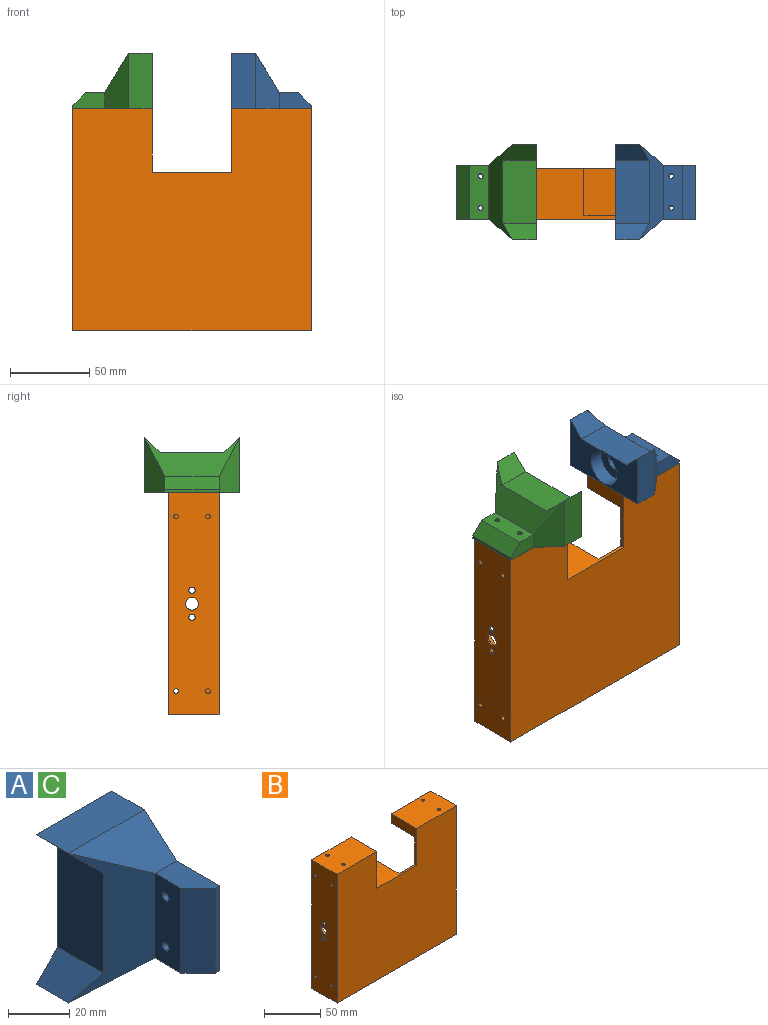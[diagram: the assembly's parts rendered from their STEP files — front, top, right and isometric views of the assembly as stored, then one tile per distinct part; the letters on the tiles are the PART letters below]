
ASSEMBLY  parts=3 mates=2
PART A: 21 faces, bbox 35x50x60 mm
  f0: plane 20x10mm, normal (0,0,-1), area 168mm2, adj f1,f2,f3,f4,f5
  f1: plane 34x2mm, normal (0,-1,0), area 68mm2, adj f0,f2,f3,f6
  f2: plane 34x8mm, normal (-0.71,-0.71,0), area 384.7mm2, adj f0,f1,f4,f6
  f3: plane 60x50mm, normal (1,0,0), area 2270.9mm2, adj f0,f1,f5,f6,f7,f8,f9,f10
  f4: plane 34x12mm, normal (-1,0,0), area 393.9mm2, adj f0,f2,f6,f11,f12,f13
  f5: plane 35x15mm, normal (0,-0.65,-0.76), area 446.6mm2, adj f0,f3,f8,f13
  f6: plane 20x10mm, normal (0,0,1), area 168mm2, adj f1,f2,f3,f4,f10
  f7: plane 60x35mm, normal (0,1,0), area 1184.5mm2, adj f3,f8,f9,f14,f15,f16,f17
  f8: plane 35x15mm, normal (0,0,-1), area 525mm2, adj f3,f5,f7,f14
  f9: plane 35x15mm, normal (0,0,1), area 525mm2, adj f3,f7,f10,f16
  f10: plane 35x15mm, normal (0,-0.65,0.76), area 446.6mm2, adj f3,f6,f9,f13
  f11: cylinder r=1.5mm len=10mm, axis (1,0,0), area 94.2mm2, adj f3,f4
  f12: cylinder r=1.5mm len=10mm, axis (1,0,0), area 94.2mm2, adj f3,f4
  f13: plane 60x25mm, normal (-0.51,-0.86,0), area 787.2mm2, adj f4,f5,f10,f14,f15,f16
  f14: plane 21x10mm, normal (-0.71,0,0.71), area 254.6mm2, adj f7,f8,f13,f15
  f15: plane 40x21mm, normal (-1,0,0), area 840mm2, adj f7,f13,f14,f16
  f16: plane 21x10mm, normal (-0.71,0,-0.71), area 254.6mm2, adj f7,f9,f13,f15
  f17: cylinder r=11.5mm len=23mm, axis (0,1,0), area 650.3mm2, adj f7,f18
  f18: plane 23x23mm, normal (0,1,0), area 336.9mm2, adj f17,f19
  f19: cylinder r=5mm len=15mm, axis (0,1,0), area 471.2mm2, adj f18,f20
  f20: plane 10x10mm, normal (0,1,0), area 78.5mm2, adj f19
PART B: 57 faces, bbox 150x32x140 mm
  f0: plane 150x140mm, normal (0,-1,0), area 19000mm2, adj f1,f2,f3,f4,f5,f6,f46,f47
  f1: plane 50x32mm, normal (0,0,1), area 1585.9mm2, adj f0,f6,f7,f8,f46,f48
  f2: plane 40x32mm, normal (-1,0,0), area 380mm2, adj f0,f3,f9,f10,f47,f48
  f3: plane 50x32mm, normal (0,0,1), area 1585.9mm2, adj f0,f2,f4,f11,f12,f48
  f4: plane 140x32mm, normal (1,0,0), area 4376.3mm2, adj f0,f3,f5,f13,f14,f15,f16,f17
  f5: plane 150x32mm, normal (0,0,-1), area 4771.7mm2, adj f0,f4,f6,f20,f21,f22,f23,f48
  f6: plane 140x32mm, normal (-1,0,0), area 4376.3mm2, adj f0,f1,f5,f24,f25,f26,f27,f28
  f7: cylinder r=1.5mm len=10mm, axis (0,0,-1), area 94.2mm2, adj f1,f31
  f8: cylinder r=1.5mm len=10mm, axis (0,0,-1), area 94.2mm2, adj f1,f31
  f9: plane 130x120mm, normal (0,1,0), area 13994mm2, adj f2,f10,f31,f32,f33,f34,f35,f36
  f10: plane 40x30mm, normal (0,0,-1), area 1185.9mm2, adj f2,f9,f11,f12,f34,f48
  f11: cylinder r=1.5mm len=10mm, axis (0,0,-1), area 94.2mm2, adj f3,f10
  f12: cylinder r=1.5mm len=10mm, axis (0,0,-1), area 94.2mm2, adj f3,f10
  f13: cylinder r=1.5mm len=10mm, axis (-1,0,0), area 94.2mm2, adj f4,f34
  f14: cylinder r=4mm len=8mm, axis (-1,0,0), area 25.1mm2, adj f4,f41
  f15: cylinder r=2mm len=4mm, axis (-1,0,0), area 12.6mm2, adj f4,f41
  f16: cylinder r=1.5mm len=10mm, axis (-1,0,0), area 94.2mm2, adj f4,f34
  f17: cylinder r=1.5mm len=10mm, axis (-1,0,0), area 94.2mm2, adj f4,f34
  f18: cylinder r=2mm len=4mm, axis (-1,0,0), area 12.6mm2, adj f4,f41
  f19: cylinder r=1.5mm len=10mm, axis (-1,0,0), area 94.2mm2, adj f4,f34
  f20: cylinder r=1.5mm len=10mm, axis (0,0,-1), area 94.2mm2, adj f5,f33
  f21: cylinder r=1.5mm len=10mm, axis (0,0,-1), area 94.2mm2, adj f5,f33
  f22: cylinder r=1.5mm len=10mm, axis (0,0,-1), area 94.2mm2, adj f5,f33
  f23: cylinder r=1.5mm len=10mm, axis (0,0,-1), area 94.2mm2, adj f5,f33
  f24: cylinder r=4mm len=8mm, axis (-1,0,0), area 25.1mm2, adj f6,f42
  f25: cylinder r=2mm len=4mm, axis (-1,0,0), area 12.6mm2, adj f6,f42
  f26: cylinder r=1.5mm len=10mm, axis (-1,0,0), area 94.2mm2, adj f6,f32
  f27: cylinder r=1.5mm len=10mm, axis (-1,0,0), area 94.2mm2, adj f6,f32
  f28: cylinder r=2mm len=4mm, axis (-1,0,0), area 12.6mm2, adj f6,f42
  f29: cylinder r=1.5mm len=10mm, axis (-1,0,0), area 94.2mm2, adj f6,f32
  f30: cylinder r=1.5mm len=10mm, axis (-1,0,0), area 94.2mm2, adj f6,f32
  f31: plane 39x30mm, normal (0,0,-1), area 1155.9mm2, adj f7,f8,f9,f32,f38,f48
  f32: plane 120x30mm, normal (1,0,0), area 3040.8mm2, adj f9,f26,f27,f29,f30,f31,f33,f43
  f33: plane 130x30mm, normal (0,0,1), area 3861.7mm2, adj f9,f20,f21,f22,f23,f32,f34,f35
  f34: plane 120x30mm, normal (-1,0,0), area 3040.8mm2, adj f9,f10,f13,f16,f17,f19,f33,f45
  f35: plane 45x10mm, normal (1,0,0), area 450mm2, adj f9,f33,f36,f44
  f36: plane 10x1mm, normal (0,0,1), area 10mm2, adj f9,f35,f37,f44
  f37: plane 45x10mm, normal (-1,0,0), area 450mm2, adj f9,f33,f36,f44
  f38: plane 31x30mm, normal (-1,0,0), area 930mm2, adj f9,f31,f39,f48
  f39: plane 31x30mm, normal (0,0,-1), area 930mm2, adj f9,f38,f40,f48
  f40: plane 30x1mm, normal (1,0,0), area 30mm2, adj f9,f39,f47,f48
  f41: plane 26x26mm, normal (-1,0,0), area 455.5mm2, adj f14,f15,f18,f45
  f42: plane 26x26mm, normal (1,0,0), area 455.5mm2, adj f24,f25,f28,f43
  f43: cylinder r=13mm len=26mm, axis (1,0,0), area 735.1mm2, adj f32,f42
  f44: plane 45x1mm, normal (0,1,0), area 45mm2, adj f33,f35,f36,f37
  f45: cylinder r=13mm len=26mm, axis (-1,0,0), area 735.1mm2, adj f34,f41
  f46: plane 40x32mm, normal (1,0,0), area 1280mm2, adj f0,f1,f47,f48
  f47: plane 50x32mm, normal (0,0,1), area 1000mm2, adj f0,f2,f9,f40,f46,f48
  f48: plane 150x140mm, normal (0,1,0), area 4932.7mm2, adj f1,f2,f3,f4,f5,f6,f10,f31
  f49: cylinder r=1.5mm len=5mm, axis (0,1,0), area 47.1mm2, adj f48,f50
  f50: plane 3x3mm, normal (0,1,0), area 7.1mm2, adj f49
  f51: cylinder r=1.5mm len=5mm, axis (0,1,0), area 47.1mm2, adj f48,f52
  f52: plane 3x3mm, normal (0,1,0), area 7.1mm2, adj f51
  f53: cylinder r=1.5mm len=5mm, axis (0,1,0), area 47.1mm2, adj f48,f54
  f54: plane 3x3mm, normal (0,1,0), area 7.1mm2, adj f53
  f55: cylinder r=1.5mm len=5mm, axis (0,1,0), area 47.1mm2, adj f48,f56
  f56: plane 3x3mm, normal (0,1,0), area 7.1mm2, adj f55
PART C: same geometry as A
PLACE A rot(axis=(-0.58,0.58,0.58),120deg) t=(100,-13,35)mm
PLACE B at identity
PLACE C rot(axis=(0.58,0.58,-0.58),120deg) t=(50,47,35)mm
MATE fastened A.f11 <-> B.f12  axis (0,0,-1) through (135,7,0)mm
MATE fastened C.f12 <-> B.f7  axis (0,0,-1) through (15,7,0)mm
